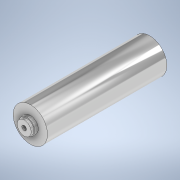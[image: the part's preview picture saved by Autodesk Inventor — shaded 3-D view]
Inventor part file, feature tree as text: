
AUTODESK INVENTOR PART (.ipt)
format: ipt  version: 2022 (Build 260153000, 153)  size: 135,168 bytes
history: native  units: mm
features: extrude x4, sketch x4, mirror x1
ambient origin geometry x8: Origin, YZ Plane, XZ Plane, XY Plane, X Axis, Y Axis, Z Axis, Center Point
bodies: Solid1 (feature_tree)
feature tree (9):
  extrude  "Base_Shell"  Depth=132.0mm
  extrude  "Terminal_Shell"  Depth=17.5mm
  extrude  "Terminal"  TaperAngle=0.0deg  [1 undecoded]
  extrude  "M5_Terminal_Screw_hole"  Depth=3.0mm
  mirror  "Mirror1"
  sketch  "Sketch1"  dims[d0=38.0mm d1=132.0mm]
  sketch  "Sketch2"  dims[d2=0.0mm d3=17.5mm]
  sketch  "Sketch3"  dims[d4=3.8mm d5=0.0mm]
  sketch  "Sketch4"  dims[d6=15.5mm d7=3.0mm d8=0.0mm d9=5.0mm d10=5.0mm d11=0.0mm]
note: 1 required parameter value undecoded (feature->parameter linkage not recoverable at this tier; creation-order binding heuristic only, values carry confidence <= 0.55)
